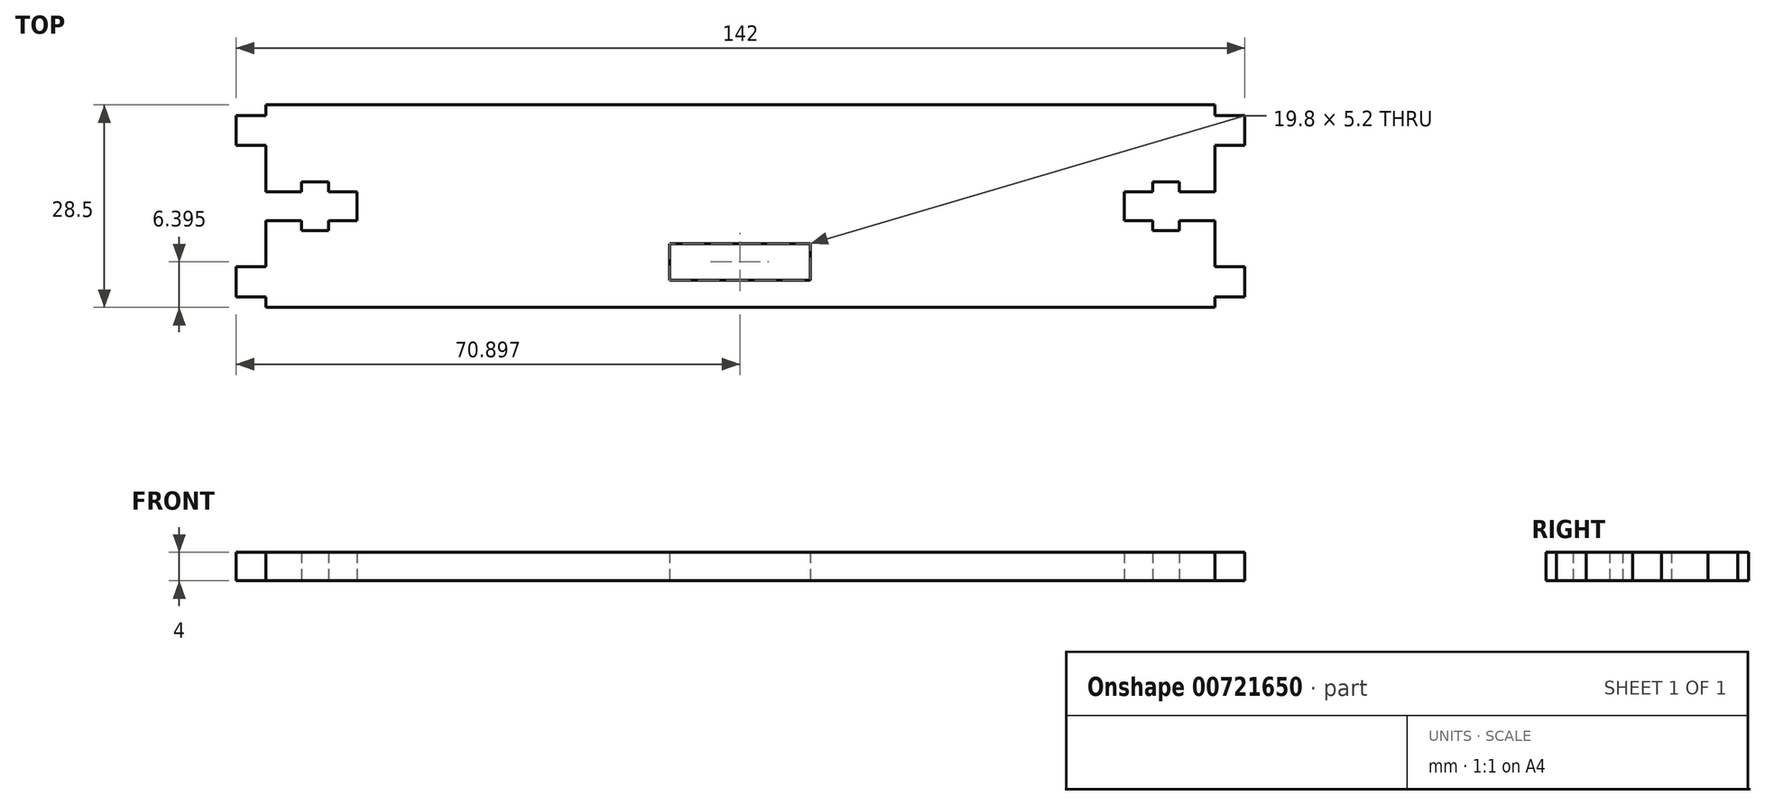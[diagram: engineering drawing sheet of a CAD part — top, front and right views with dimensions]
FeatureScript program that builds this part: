
annotation { "Feature Type Name" : "Feature", "Feature Type Description" : "" }
export const myFeature = defineFeature(function(context is Context, id is Id, definition is map)
    precondition{}
    {
        {
            var Q0;
            Q0=qCreatedBy(makeId("Top.planeOp"),FACE);
            var sketch = newSketch(context, id + "F0", { "sketchPlane" : qUnion([Q0])});
            skLineSegment(sketch, "E0.bottom", {"start": v(-93.7, 8.97) * mm, "end": v(39.9, 8.97) * mm});
            skLineSegment(sketch, "E0.top", {"start": v(-93.7, -19.53) * mm, "end": v(39.9, -19.53) * mm});
            skLineSegment(sketch, "E0.left", {"start": v(-97.9, 7.47) * mm, "end": v(-97.9, 3.27) * mm});
            skLineSegment(sketch, "E0.right", {"start": v(44.1, 7.47) * mm, "end": v(44.1, 3.27) * mm});
            skLineSegment(sketch, "E1", {"start": v(-97.9, -18.03) * mm, "end": v(-93.7, -18.03) * mm});
            skLineSegment(sketch, "E2", {"start": v(-97.9, 7.47) * mm, "end": v(-93.7, 7.47) * mm});
            skLineSegment(sketch, "E3", {"start": v(39.9, 8.97) * mm, "end": v(39.9, 7.47) * mm});
            skLineSegment(sketch, "E4", {"start": v(-93.7, 8.97) * mm, "end": v(-93.7, 7.47) * mm});
            skLineSegment(sketch, "E5", {"start": v(-93.7, -7.33) * mm, "end": v(-88.7, -7.33) * mm});
            skLineSegment(sketch, "E6", {"start": v(-93.7, -3.23) * mm, "end": v(-88.7, -3.23) * mm});
            skLineSegment(sketch, "E7", {"start": v(-97.9, -13.83) * mm, "end": v(-93.7, -13.83) * mm});
            skLineSegment(sketch, "E8", {"start": v(-97.9, 3.27) * mm, "end": v(-93.7, 3.27) * mm});
            skLineSegment(sketch, "E9.trimOffspring", {"start": v(-97.9, -13.83) * mm, "end": v(-97.9, -18.03) * mm});
            skLineSegment(sketch, "E10.trimOffspring", {"start": v(44.1, -13.83) * mm, "end": v(44.1, -18.03) * mm});
            skLineSegment(sketch, "E11.trimOffspring", {"start": v(-80.9, -3.23) * mm, "end": v(-80.9, -7.33) * mm});
            skLineSegment(sketch, "E12.trimOffspring", {"start": v(27.1, -3.23) * mm, "end": v(27.1, -7.33) * mm});
            skLineSegment(sketch, "E13.trimOffspring", {"start": v(-93.7, -7.33) * mm, "end": v(-93.7, -13.83) * mm});
            skLineSegment(sketch, "E14.trimOffspring", {"start": v(39.9, 3.27) * mm, "end": v(39.9, -3.23) * mm});
            skLineSegment(sketch, "E15.trimOffspring", {"start": v(39.9, -7.33) * mm, "end": v(39.9, -13.83) * mm});
            skLineSegment(sketch, "E16.trimOffspring", {"start": v(39.9, -18.03) * mm, "end": v(39.9, -19.53) * mm});
            skLineSegment(sketch, "E17", {"start": v(-88.7, -8.73) * mm, "end": v(-84.9, -8.73) * mm});
            skLineSegment(sketch, "E18", {"start": v(-88.7, -1.83) * mm, "end": v(-84.9, -1.83) * mm});
            skLineSegment(sketch, "E19.trimOffspring", {"start": v(39.9, -18.03) * mm, "end": v(44.1, -18.03) * mm});
            skLineSegment(sketch, "E20.trimOffspring", {"start": v(39.9, -13.83) * mm, "end": v(44.1, -13.83) * mm});
            skLineSegment(sketch, "E21.trimOffspring", {"start": v(-93.7, -18.03) * mm, "end": v(-93.7, -19.53) * mm});
            skLineSegment(sketch, "E22.trimOffspring", {"start": v(39.9, 3.27) * mm, "end": v(44.1, 3.27) * mm});
            skLineSegment(sketch, "E23.trimOffspring", {"start": v(-93.7, 3.27) * mm, "end": v(-93.7, -3.23) * mm});
            skLineSegment(sketch, "E24.trimOffspring", {"start": v(27.1, -3.23) * mm, "end": v(31.1, -3.23) * mm});
            skLineSegment(sketch, "E25.trimOffspring", {"start": v(27.1, -7.33) * mm, "end": v(31.1, -7.33) * mm});
            skLineSegment(sketch, "E26", {"start": v(-84.9, -1.83) * mm, "end": v(-84.9, -3.23) * mm});
            skLineSegment(sketch, "E27", {"start": v(-88.7, -1.83) * mm, "end": v(-88.7, -3.23) * mm});
            skLineSegment(sketch, "E28.trimOffspring", {"start": v(-84.9, -3.23) * mm, "end": v(-80.9, -3.23) * mm});
            skLineSegment(sketch, "E29.trimOffspring", {"start": v(-84.9, -7.33) * mm, "end": v(-80.9, -7.33) * mm});
            skLineSegment(sketch, "E30.trimOffspring", {"start": v(-84.9, -7.33) * mm, "end": v(-84.9, -8.73) * mm});
            skLineSegment(sketch, "E31.trimOffspring", {"start": v(-88.7, -7.33) * mm, "end": v(-88.7, -8.73) * mm});
            skLineSegment(sketch, "E32", {"start": v(34.9, -1.83) * mm, "end": v(34.9, -3.23) * mm});
            skLineSegment(sketch, "E33", {"start": v(31.1, -1.83) * mm, "end": v(31.1, -3.23) * mm});
            skLineSegment(sketch, "E34.trimOffspring", {"start": v(34.9, -3.23) * mm, "end": v(39.9, -3.23) * mm});
            skLineSegment(sketch, "E35.trimOffspring", {"start": v(34.9, -7.33) * mm, "end": v(39.9, -7.33) * mm});
            skLineSegment(sketch, "E36.trimOffspring", {"start": v(34.9, -7.33) * mm, "end": v(34.9, -8.73) * mm});
            skLineSegment(sketch, "E37.trimOffspring", {"start": v(31.1, -7.33) * mm, "end": v(31.1, -8.73) * mm});
            skLineSegment(sketch, "E38.trimOffspring", {"start": v(31.1, -8.73) * mm, "end": v(34.9, -8.73) * mm});
            skLineSegment(sketch, "E39.trimOffspring", {"start": v(31.1, -1.83) * mm, "end": v(34.9, -1.83) * mm});
            skLineSegment(sketch, "E40.bottom", {"start": v(-36.9, -10.53) * mm, "end": v(-17.1, -10.53) * mm});
            skLineSegment(sketch, "E40.top", {"start": v(-36.9, -15.73) * mm, "end": v(-17.1, -15.73) * mm});
            skLineSegment(sketch, "E40.left", {"start": v(-36.9, -10.53) * mm, "end": v(-36.9, -15.73) * mm});
            skLineSegment(sketch, "E40.right", {"start": v(-17.1, -10.53) * mm, "end": v(-17.1, -15.73) * mm});
            skLineSegment(sketch, "E41.trimOffspring", {"start": v(39.9, 7.47) * mm, "end": v(44.1, 7.47) * mm});
            skSolve(sketch);
        }
        {
            var Q0;
            Q0=makeQuery(id+"F0.imprint","IMPRINT",FACE,{"disambiguationData":[TD([[makeQuery(id+"F0.imprint","IMPRINT",EDGE,{"derivedFrom":sQuery(id+"F0.wireOp",EDGE,"E0.bottom")}),-1.0]])]});
            extrude(context, id + "F1", {"entities" : qUnion([Q0]), "depth" : (4) * mm, "offsetDistance" : 25 * mm});
        }
    });
